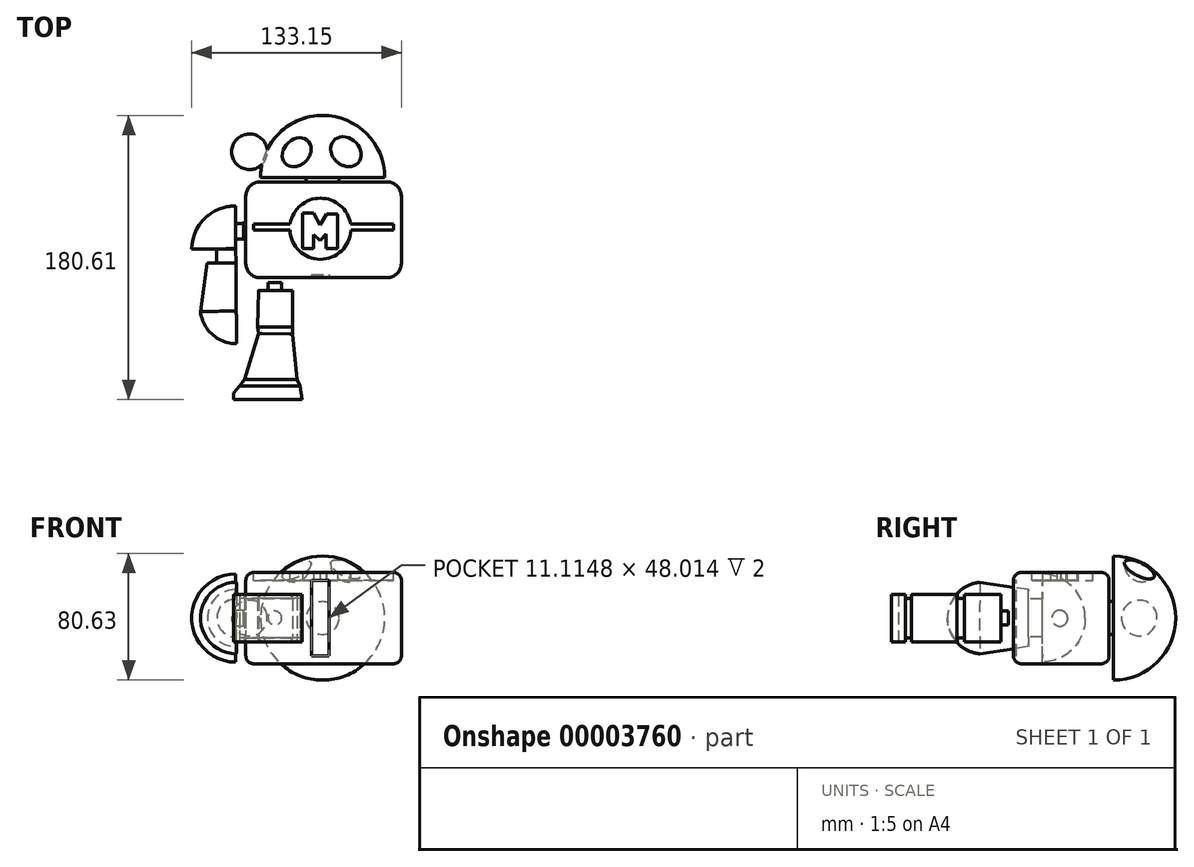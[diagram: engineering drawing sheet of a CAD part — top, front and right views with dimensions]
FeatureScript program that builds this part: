
annotation { "Feature Type Name" : "Feature", "Feature Type Description" : "" }
export const myFeature = defineFeature(function(context is Context, id is Id, definition is map)
    precondition{}
    {
        {
            var Q0;
            Q0=qCreatedBy(makeId("Top.planeOp"),FACE);
            var sketch = newSketch(context, id + "F0", { "sketchPlane" : qUnion([Q0])});
            skArc(sketch, "E0", {"start": v(39.44, 0) * mm, "mid": v(39.43, 0.3) * mm, "end": v(39.43, 0.59) * mm});
            skLineSegment(sketch, "E1", {"start": v(-39.44, 0) * mm, "end": v(0, 0) * mm});
            skLineSegment(sketch, "E2", {"start": v(0, 0) * mm, "end": v(0, 39.44) * mm});
            skArc(sketch, "E3", {"start": v(0, 39.44) * mm, "mid": v(-27.88, 27.88) * mm, "end": v(-39.44, 0) * mm});
            skSolve(sketch);
        }
        {
            var Q0;
            Q0=makeQuery(id+"F0.imprint","IMPRINT",FACE,{"disambiguationData":[TD([[makeQuery(id+"F0.imprint","IMPRINT",EDGE,{"derivedFrom":sQuery(id+"F0.wireOp",EDGE,"E1")}),1.0]])]});
            var Q1;
            Q1=sQuery(id+"F0.wireOp",EDGE,"E2");
            revolve(context, id + "F1", {"entities" : qUnion([Q0]), "axis" : qUnion([Q1]), "revolveType" : RevolveType.FULL});
        }
        {
            var Q0;
            Q0=qCreatedBy(makeId("Top.planeOp"),FACE);
            var sketch = newSketch(context, id + "F2", { "sketchPlane" : qUnion([Q0])});
            skCircle(sketch, "E4", {"center": v(-46.45, 16.3) * mm, "radius": 11.3 * mm});
            skLineSegment(sketch, "E5", {"start": v(-46.45, 27.6) * mm, "end": v(-46.45, 5) * mm});
            skSolve(sketch);
        }
        {
            var Q0;
            {var subQ0=sQuery(id+"F2.wireOp",EDGE,"E5");Q0=makeQuery(id+"F2.imprint","IMPRINT",FACE,{"disambiguationData":[TD([[makeQuery(id+"F2.imprint","IMPRINT",EDGE,{"derivedFrom":subQ0}),1.0]])]});}
            var Q1;
            Q1=sQuery(id+"F2.wireOp",EDGE,"E4");
            var Q2;
            Q2=sQuery(id+"F2.wireOp",EDGE,"E5");
            revolve(context, id + "F3", {"entities" : qUnion([Q0]), "surfaceEntities" : qUnion([Q1]), "axis" : qUnion([Q2]), "revolveType" : RevolveType.FULL});
        }
        {
            var Q0;
            Q0=makeQuery(id+"F1.opRevolve","SWEPT_BODY",BODY,{"disambiguationData":[OSD([sQuery(id+"F0.wireOp",EDGE,"E1"),sQuery(id+"F0.wireOp",EDGE,"E2"),sQuery(id+"F0.wireOp",EDGE,"E3")])]});
            transform(context, id + "F4", {"entities" : qUnion([Q0]), "transformType" : TransformType.COPY});
        }
        {
            var Q0;
            Q0=makeQuery(id+"F4.opPattern","COPY",BODY,{"derivedFrom":makeQuery(id+"F1.opRevolve","SWEPT_BODY",BODY,{"disambiguationData":[OSD([sQuery(id+"F0.wireOp",EDGE,"E1"),sQuery(id+"F0.wireOp",EDGE,"E2"),sQuery(id+"F0.wireOp",EDGE,"E3")])]}),"instanceName":"1"});
            var Q1;
            Q1=qCreatedBy(makeId("Origin.pointOp"),VERTEX);
            transform(context, id + "F5", {"entities" : qUnion([Q0]), "transformType" : TransformType.SCALE_UNIFORMLY, "scale" : 0.2, "makeCopy" : false, "scalePoint" : qUnion([Q1])});
        }
        {
            var Q0;
            Q0=makeQuery(id+"F3.opRevolve","SWEPT_BODY",BODY,{"disambiguationData":[OSD([sQuery(id+"F2.wireOp",EDGE,"E4"),sQuery(id+"F2.wireOp",EDGE,"E5")])]});
            transform(context, id + "F6", {"entities" : qUnion([Q0]), "transformType" : TransformType.TRANSLATION_3D, "dx" : 27.9 * mm, "dy" : 1.83 * mm, "dz" : 34.34 * mm, "makeCopy" : true});
        }
        {
            var Q0;
            Q0=makeQuery(id+"F6.opPattern","COPY",BODY,{"derivedFrom":makeQuery(id+"F3.opRevolve","SWEPT_BODY",BODY,{"disambiguationData":[OSD([sQuery(id+"F2.wireOp",EDGE,"E4"),sQuery(id+"F2.wireOp",EDGE,"E5")])]}),"instanceName":"1"});
            transform(context, id + "F7", {"entities" : qUnion([Q0]), "transformType" : TransformType.TRANSLATION_3D, "dx" : 35 * mm, "dy" : 0 * mm, "dz" : 0 * mm, "makeCopy" : true});
        }
        {
            var Q0;
            Q0=makeQuery(id+"F6.opPattern","COPY",BODY,{"derivedFrom":makeQuery(id+"F3.opRevolve","SWEPT_BODY",BODY,{"disambiguationData":[OSD([sQuery(id+"F2.wireOp",EDGE,"E4"),sQuery(id+"F2.wireOp",EDGE,"E5")])]}),"instanceName":"1"});
            var Q1;
            Q1=makeQuery(id+"F7.opPattern","COPY",BODY,{"derivedFrom":makeQuery(id+"F6.opPattern","COPY",BODY,{"derivedFrom":makeQuery(id+"F3.opRevolve","SWEPT_BODY",BODY,{"disambiguationData":[OSD([sQuery(id+"F2.wireOp",EDGE,"E4"),sQuery(id+"F2.wireOp",EDGE,"E5")])]}),"instanceName":"1"}),"instanceName":"1"});
            var Q2;
            Q2=makeQuery(id+"F1.opRevolve","SWEPT_BODY",BODY,{"disambiguationData":[OSD([sQuery(id+"F0.wireOp",EDGE,"E1"),sQuery(id+"F0.wireOp",EDGE,"E2"),sQuery(id+"F0.wireOp",EDGE,"E3")])]});
            booleanBodies(context, id + "F8", {"operationType" : BooleanOperationType.SUBTRACTION, "tools" : qUnion([Q0, Q1]), "targets" : qUnion([Q2])});
        }
        {
            var Q0;
            Q0=qCreatedBy(makeId("Top.planeOp"),FACE);
            var sketch = newSketch(context, id + "F9", { "sketchPlane" : qUnion([Q0])});
            skLineSegment(sketch, "E6.bottom", {"start": v(-39.75, -2.85) * mm, "end": v(41.03, -2.85) * mm});
            skLineSegment(sketch, "E6.top", {"start": v(-39.75, -63.63) * mm, "end": v(41.03, -63.63) * mm});
            skLineSegment(sketch, "E6.left", {"start": v(-48.75, -11.85) * mm, "end": v(-48.75, -54.63) * mm});
            skLineSegment(sketch, "E6.right", {"start": v(50.03, -11.85) * mm, "end": v(50.03, -54.63) * mm});
            skPoint(sketch, "E7.visualSharp", {"position": v(-48.75, -2.85) * mm});
            skArc(sketch, "E7.filletArc", {"start": v(-39.75, -2.85) * mm, "mid": v(-46.12, -5.49) * mm, "end": v(-48.75, -11.85) * mm});
            skPoint(sketch, "E8.visualSharp", {"position": v(50.03, -2.85) * mm});
            skArc(sketch, "E8.filletArc", {"start": v(50.03, -11.85) * mm, "mid": v(47.4, -5.49) * mm, "end": v(41.03, -2.85) * mm});
            skPoint(sketch, "E9.visualSharp", {"position": v(50.03, -63.63) * mm});
            skArc(sketch, "E9.filletArc", {"start": v(41.03, -63.63) * mm, "mid": v(47.4, -61) * mm, "end": v(50.03, -54.63) * mm});
            skPoint(sketch, "E10.visualSharp", {"position": v(-48.75, -63.63) * mm});
            skArc(sketch, "E10.filletArc", {"start": v(-48.75, -54.63) * mm, "mid": v(-46.12, -61) * mm, "end": v(-39.75, -63.63) * mm});
            skSolve(sketch);
        }
        {
            var Q0;
            Q0=makeQuery(id+"F9.imprint","IMPRINT",FACE,{"disambiguationData":[TD([[makeQuery(id+"F9.imprint","IMPRINT",EDGE,{"derivedFrom":sQuery(id+"F9.wireOp",EDGE,"E6.bottom")}),-1.0]])]});
            extrude(context, id + "F10", {"entities" : qUnion([Q0]), "endBound" : BoundingType.SYMMETRIC, "depth" : 58 * mm});
        }
        {
            var Q0;
            Q0=qCreatedBy(makeId("Top.planeOp"),FACE);
            var sketch = newSketch(context, id + "F11", { "sketchPlane" : qUnion([Q0])});
            skArc(sketch, "E11", {"start": v(-55.4, -18.13) * mm, "mid": v(-74.92, -26.07) * mm, "end": v(-83.12, -45.48) * mm});
            skLineSegment(sketch, "E12", {"start": v(-83.12, -45.48) * mm, "end": v(-67.17, -45.48) * mm});
            skLineSegment(sketch, "E13", {"start": v(-67.17, -45.48) * mm, "end": v(-67.17, -54.36) * mm});
            skLineSegment(sketch, "E14", {"start": v(-67.17, -54.36) * mm, "end": v(-73.25, -54.36) * mm});
            skLineSegment(sketch, "E15", {"start": v(-73.25, -54.36) * mm, "end": v(-77.56, -85.1) * mm});
            skArc(sketch, "E16", {"start": v(-77.56, -85.1) * mm, "mid": v(-70.06, -99.74) * mm, "end": v(-54.64, -105.5) * mm});
            skLineSegment(sketch, "E17", {"start": v(-54.64, -105.5) * mm, "end": v(-55.4, -18.13) * mm});
            skSolve(sketch);
        }
        {
            var Q0;
            Q0=makeQuery(id+"F11.imprint","IMPRINT",FACE,{"disambiguationData":[TD([[makeQuery(id+"F11.imprint","IMPRINT",EDGE,{"derivedFrom":sQuery(id+"F11.wireOp",EDGE,"E11")}),1.0]])]});
            var Q1;
            Q1=sQuery(id+"F11.wireOp",EDGE,"E17");
            revolve(context, id + "F12", {"entities" : qUnion([Q0]), "axis" : qUnion([Q1]), "revolveType" : RevolveType.SYMMETRIC, "angle" : 180 * degree});
        }
        {
            var Q0;
            Q0=qCreatedBy(makeId("Top.planeOp"),FACE);
            var sketch = newSketch(context, id + "F13", { "sketchPlane" : qUnion([Q0])});
            skLineSegment(sketch, "E18", {"start": v(-40.54, -71.66) * mm, "end": v(-19.06, -71.66) * mm});
            skLineSegment(sketch, "E19", {"start": v(-19.06, -71.66) * mm, "end": v(-19.06, -94.9) * mm});
            skLineSegment(sketch, "E20", {"start": v(-19.06, -94.9) * mm, "end": v(-41.36, -94.9) * mm});
            skLineSegment(sketch, "E21", {"start": v(-41.36, -94.9) * mm, "end": v(-40.54, -71.66) * mm});
            skLineSegment(sketch, "E22", {"start": v(-40.54, -99.07) * mm, "end": v(-49.65, -128.28) * mm});
            skLineSegment(sketch, "E23", {"start": v(-49.65, -128.28) * mm, "end": v(-16.26, -128.28) * mm});
            skLineSegment(sketch, "E24", {"start": v(-16.26, -128.28) * mm, "end": v(-19.1, -99.53) * mm});
            skLineSegment(sketch, "E25", {"start": v(-19.1, -99.53) * mm, "end": v(-40.54, -99.07) * mm});
            skLineSegment(sketch, "E26", {"start": v(-14.37, -132.38) * mm, "end": v(-52.7, -132.38) * mm});
            skLineSegment(sketch, "E27", {"start": v(-52.7, -132.38) * mm, "end": v(-56.6, -136.81) * mm});
            skLineSegment(sketch, "E28", {"start": v(-56.6, -136.81) * mm, "end": v(-56.6, -141.17) * mm});
            skLineSegment(sketch, "E29", {"start": v(-56.6, -141.17) * mm, "end": v(-13.15, -141.17) * mm});
            skLineSegment(sketch, "E30", {"start": v(-13.15, -141.17) * mm, "end": v(-14.37, -132.38) * mm});
            skLineSegment(sketch, "E31", {"start": v(-41.36, -94.9) * mm, "end": v(-40.54, -99.07) * mm});
            skLineSegment(sketch, "E32", {"start": v(-49.65, -128.28) * mm, "end": v(-52.7, -132.38) * mm});
            skLineSegment(sketch, "E33", {"start": v(-14.37, -132.38) * mm, "end": v(-16.26, -128.28) * mm});
            skLineSegment(sketch, "E34", {"start": v(-19.1, -99.53) * mm, "end": v(-19.06, -94.9) * mm});
            skSolve(sketch);
        }
        {
            var Q0;
            Q0=makeQuery(id+"F13.imprint","IMPRINT",FACE,{"disambiguationData":[TD([[makeQuery(id+"F13.imprint","IMPRINT",EDGE,{"derivedFrom":sQuery(id+"F13.wireOp",EDGE,"E26")}),1.0]])]});
            var Q1;
            Q1=makeQuery(id+"F13.imprint","IMPRINT",FACE,{"disambiguationData":[TD([[makeQuery(id+"F13.imprint","IMPRINT",EDGE,{"derivedFrom":sQuery(id+"F13.wireOp",EDGE,"E22")}),1.0]])]});
            var Q2;
            Q2=makeQuery(id+"F13.imprint","IMPRINT",FACE,{"disambiguationData":[TD([[makeQuery(id+"F13.imprint","IMPRINT",EDGE,{"derivedFrom":sQuery(id+"F13.wireOp",EDGE,"E18")}),-1.0]])]});
            extrude(context, id + "F14", {"entities" : qUnion([Q0, Q1, Q2]), "endBound" : BoundingType.SYMMETRIC, "depth" : 30 * mm});
        }
        {
            var Q0;
            Q0=makeQuery(id+"F13.imprint","IMPRINT",FACE,{"disambiguationData":[TD([[makeQuery(id+"F13.imprint","IMPRINT",EDGE,{"derivedFrom":sQuery(id+"F13.wireOp",EDGE,"E20")}),1.0]])]});
            var Q1;
            Q1=makeQuery(id+"F13.imprint","IMPRINT",FACE,{"disambiguationData":[TD([[makeQuery(id+"F13.imprint","IMPRINT",EDGE,{"derivedFrom":sQuery(id+"F13.wireOp",EDGE,"E23")}),-1.0]])]});
            extrude(context, id + "F15", {"entities" : qUnion([Q0, Q1]), "endBound" : BoundingType.SYMMETRIC, "depth" : 25 * mm});
        }
        {
            var Q0;
            Q0=makeQuery(id+"F10.opExtrude","CAP_FACE",FACE,{"disambiguationData":[OSD([sQuery(id+"F9.wireOp",EDGE,"E6.bottom"),sQuery(id+"F9.wireOp",EDGE,"E6.top"),sQuery(id+"F9.wireOp",EDGE,"E6.left"),sQuery(id+"F9.wireOp",EDGE,"E6.right"),sQuery(id+"F9.wireOp",EDGE,"E7.filletArc"),sQuery(id+"F9.wireOp",EDGE,"E8.filletArc"),sQuery(id+"F9.wireOp",EDGE,"E9.filletArc"),sQuery(id+"F9.wireOp",EDGE,"E10.filletArc")])],"isStart":false});
            fillet(context, id + "F16", {"entities" : qUnion([Q0]), "radius" : 5 * mm, "tangentPropagation" : true, "allowEdgeOverflow" : false});
        }
        {
            var Q0;
            Q0=makeQuery(id+"F10.opExtrude","CAP_FACE",FACE,{"disambiguationData":[OSD([sQuery(id+"F9.wireOp",EDGE,"E6.bottom"),sQuery(id+"F9.wireOp",EDGE,"E6.top"),sQuery(id+"F9.wireOp",EDGE,"E6.left"),sQuery(id+"F9.wireOp",EDGE,"E6.right"),sQuery(id+"F9.wireOp",EDGE,"E7.filletArc"),sQuery(id+"F9.wireOp",EDGE,"E8.filletArc"),sQuery(id+"F9.wireOp",EDGE,"E9.filletArc"),sQuery(id+"F9.wireOp",EDGE,"E10.filletArc")])],"isStart":true});
            fillet(context, id + "F17", {"entities" : qUnion([Q0]), "radius" : 5 * mm, "tangentPropagation" : true, "allowEdgeOverflow" : false});
        }
        {
            var Q0;
            Q0=makeQuery(id+"F14.opExtrude","CAP_EDGE",EDGE,{"disambiguationData":[OSD([sQuery(id+"F13.wireOp",EDGE,"E21")])],"isStart":false});
            var Q1;
            Q1=makeQuery(id+"F14.opExtrude","CAP_EDGE",EDGE,{"disambiguationData":[OSD([sQuery(id+"F13.wireOp",EDGE,"E19")])],"isStart":false});
            var Q2;
            Q2=makeQuery(id+"F14.opExtrude","CAP_EDGE",EDGE,{"disambiguationData":[OSD([sQuery(id+"F13.wireOp",EDGE,"E19")])],"isStart":true});
            var Q3;
            Q3=makeQuery(id+"F14.opExtrude","CAP_EDGE",EDGE,{"disambiguationData":[OSD([sQuery(id+"F13.wireOp",EDGE,"E21")])],"isStart":true});
            fillet(context, id + "F18", {"entities" : qUnion([Q0, Q1, Q2, Q3]), "radius" : 3 * mm, "allowEdgeOverflow" : false});
        }
        {
            var Q0;
            Q0=makeQuery(id+"F14.opExtrude","CAP_EDGE",EDGE,{"disambiguationData":[OSD([sQuery(id+"F13.wireOp",EDGE,"E22")])],"isStart":false});
            var Q1;
            Q1=makeQuery(id+"F14.opExtrude","CAP_EDGE",EDGE,{"disambiguationData":[OSD([sQuery(id+"F13.wireOp",EDGE,"E24")])],"isStart":false});
            var Q2;
            Q2=makeQuery(id+"F14.opExtrude","CAP_EDGE",EDGE,{"disambiguationData":[OSD([sQuery(id+"F13.wireOp",EDGE,"E24")])],"isStart":true});
            var Q3;
            Q3=makeQuery(id+"F14.opExtrude","CAP_EDGE",EDGE,{"disambiguationData":[OSD([sQuery(id+"F13.wireOp",EDGE,"E22")])],"isStart":true});
            fillet(context, id + "F19", {"entities" : qUnion([Q0, Q1, Q2, Q3]), "radius" : 2 * mm, "allowEdgeOverflow" : false});
        }
        {
            var Q0;
            Q0=makeQuery(id+"F10.opExtrude","CAP_FACE",FACE,{"disambiguationData":[OSD([sQuery(id+"F9.wireOp",EDGE,"E6.bottom"),sQuery(id+"F9.wireOp",EDGE,"E6.top"),sQuery(id+"F9.wireOp",EDGE,"E6.left"),sQuery(id+"F9.wireOp",EDGE,"E6.right"),sQuery(id+"F9.wireOp",EDGE,"E7.filletArc"),sQuery(id+"F9.wireOp",EDGE,"E8.filletArc"),sQuery(id+"F9.wireOp",EDGE,"E9.filletArc"),sQuery(id+"F9.wireOp",EDGE,"E10.filletArc")])],"isStart":false});
            var sketch = newSketch(context, id + "F20", { "sketchPlane" : qUnion([Q0])});
            skCircle(sketch, "E35", {"center": v(-1.4, -32.58) * mm, "radius": 19.4 * mm});
            skLineSegment(sketch, "E36", {"start": v(-20.56, -29.48) * mm, "end": v(-43.75, -29.48) * mm});
            skLineSegment(sketch, "E37", {"start": v(-43.75, -29.48) * mm, "end": v(-43.75, -33.24) * mm});
            skLineSegment(sketch, "E38", {"start": v(-43.75, -33.24) * mm, "end": v(-20.8, -33.24) * mm});
            skLineSegment(sketch, "E39", {"start": v(17.98, -33.48) * mm, "end": v(45.03, -33.48) * mm});
            skLineSegment(sketch, "E40", {"start": v(45.03, -33.48) * mm, "end": v(45.03, -29.48) * mm});
            skLineSegment(sketch, "E41", {"start": v(45.03, -29.48) * mm, "end": v(17.76, -29.48) * mm});
            skSolve(sketch);
        }
        {
            var Q0;
            Q0 = qSketchRegion(id + "F20", true);
            extrude(context, id + "F21", {"entities" : qUnion([Q0]), "operationType" : NewBodyOperationType.REMOVE, "oppositeDirection" : true, "depth" : 5 * mm});
        }
        {
            var Q0;
            Q0=makeQuery(id+"F21.boolean.opBoolean","COPY",FACE,{"derivedFrom":makeQuery(id+"F21.opExtrude","CAP_FACE",FACE,{"disambiguationData":[OSD([sQuery(id+"F20.wireOp",EDGE,"E35")])],"isStart":false})});
            var sketch = newSketch(context, id + "F22", { "sketchPlane" : qUnion([Q0])});
            skLineSegment(sketch, "E42", {"start": v(-12.61, -45.17) * mm, "end": v(-12.61, -22.72) * mm});
            skLineSegment(sketch, "E43", {"start": v(-12.61, -22.72) * mm, "end": v(-5.87, -22.72) * mm});
            skLineSegment(sketch, "E44", {"start": v(-5.87, -22.72) * mm, "end": v(-1.58, -30.17) * mm});
            skLineSegment(sketch, "E45", {"start": v(-1.58, -30.17) * mm, "end": v(2.66, -23.15) * mm});
            skLineSegment(sketch, "E46", {"start": v(2.66, -23.15) * mm, "end": v(9.67, -23.15) * mm});
            skLineSegment(sketch, "E47", {"start": v(9.67, -23.15) * mm, "end": v(9.67, -45.14) * mm});
            skLineSegment(sketch, "E48", {"start": v(9.67, -45.14) * mm, "end": v(2.32, -45.14) * mm});
            skLineSegment(sketch, "E49", {"start": v(2.32, -45.14) * mm, "end": v(2.32, -36.03) * mm});
            skLineSegment(sketch, "E50", {"start": v(2.32, -36.03) * mm, "end": v(-1.64, -40.08) * mm});
            skLineSegment(sketch, "E51", {"start": v(-1.64, -40.08) * mm, "end": v(-5.7, -36.1) * mm});
            skLineSegment(sketch, "E52", {"start": v(-5.7, -36.1) * mm, "end": v(-5.7, -45.17) * mm});
            skLineSegment(sketch, "E53", {"start": v(-5.7, -45.17) * mm, "end": v(-12.61, -45.17) * mm});
            skSolve(sketch);
        }
        {
            var Q0;
            Q0=makeQuery(id+"F22.imprint","IMPRINT",FACE,{"disambiguationData":[TD([[makeQuery(id+"F22.imprint","IMPRINT",EDGE,{"derivedFrom":sQuery(id+"F22.wireOp",EDGE,"E42")}),-1.0]])]});
            extrude(context, id + "F23", {"entities" : qUnion([Q0]), "operationType" : NewBodyOperationType.ADD, "depth" : 5 * mm});
        }
        {
            var Q0;
            Q0=makeQuery(id+"F12.opRevolve","CAP_FACE",FACE,{"disambiguationData":[OSD([sQuery(id+"F11.wireOp",EDGE,"E11"),sQuery(id+"F11.wireOp",EDGE,"E12"),sQuery(id+"F11.wireOp",EDGE,"E13"),sQuery(id+"F11.wireOp",EDGE,"E14"),sQuery(id+"F11.wireOp",EDGE,"E15"),sQuery(id+"F11.wireOp",EDGE,"E16"),sQuery(id+"F11.wireOp",EDGE,"E17")])],"isStart":true});
            var sketch = newSketch(context, id + "F24", { "sketchPlane" : qUnion([Q0])});
            skCircle(sketch, "E54", {"center": v(-33.72, -0.16) * mm, "radius": 5.05 * mm});
            skSolve(sketch);
        }
        {
            var Q0;
            Q0=makeQuery(id+"F24.imprint","IMPRINT",FACE,{"disambiguationData":[TD([[makeQuery(id+"F24.imprint","IMPRINT",EDGE,{"derivedFrom":sQuery(id+"F24.wireOp",EDGE,"E54")}),1.0]])]});
            extrude(context, id + "F25", {"entities" : qUnion([Q0]), "operationType" : NewBodyOperationType.ADD, "depth" : 5 * mm});
        }
        {
            var Q0;
            Q0=makeQuery(id+"F14.opExtrude","SWEPT_FACE",FACE,{"disambiguationData":[OSD([sQuery(id+"F13.wireOp",EDGE,"E18")])]});
            var sketch = newSketch(context, id + "F26", { "sketchPlane" : qUnion([Q0])});
            skCircle(sketch, "E55", {"center": v(30.37, 0) * mm, "radius": 4.4 * mm});
            skSolve(sketch);
        }
        {
            var Q0;
            Q0=makeQuery(id+"F26.imprint","IMPRINT",FACE,{"disambiguationData":[TD([[makeQuery(id+"F26.imprint","IMPRINT",EDGE,{"derivedFrom":sQuery(id+"F26.wireOp",EDGE,"E55")}),1.0]])]});
            extrude(context, id + "F27", {"entities" : qUnion([Q0]), "operationType" : NewBodyOperationType.ADD, "depth" : 5 * mm});
        }
        {
            var Q0;
            Q0=makeQuery(id+"F1.opRevolve","SWEPT_FACE",FACE,{"disambiguationData":[OSD([sQuery(id+"F0.wireOp",EDGE,"E1")])]});
            var sketch = newSketch(context, id + "F28", { "sketchPlane" : qUnion([Q0])});
            skCircle(sketch, "E56", {"center": v(0, 0) * mm, "radius": 10.44 * mm});
            skSolve(sketch);
        }
        {
            var Q0;
            Q0 = qSketchRegion(id + "F28", true);
            extrude(context, id + "F29", {"entities" : qUnion([Q0]), "operationType" : NewBodyOperationType.ADD, "depth" : 5 * mm});
        }
        {
            var Q0;
            Q0=makeQuery(id+"F10.opExtrude","SWEPT_FACE",FACE,{"disambiguationData":[OSD([sQuery(id+"F9.wireOp",EDGE,"E6.top")])]});
            var sketch = newSketch(context, id + "F30", { "sketchPlane" : qUnion([Q0])});
            skLineSegment(sketch, "E57.bottom", {"start": v(-7.02, -24) * mm, "end": v(4.1, -24) * mm});
            skLineSegment(sketch, "E57.top", {"start": v(-7.02, 24) * mm, "end": v(4.1, 24) * mm});
            skLineSegment(sketch, "E57.left", {"start": v(-7.02, -24) * mm, "end": v(-7.02, 24) * mm});
            skLineSegment(sketch, "E57.right", {"start": v(4.1, -24) * mm, "end": v(4.1, 24) * mm});
            skSolve(sketch);
        }
        {
            var Q0;
            Q0=makeQuery(id+"F30.imprint","IMPRINT",FACE,{"disambiguationData":[TD([[makeQuery(id+"F30.imprint","IMPRINT",EDGE,{"derivedFrom":sQuery(id+"F30.wireOp",EDGE,"E57.bottom")}),1.0]])]});
            extrude(context, id + "F31", {"entities" : qUnion([Q0]), "operationType" : NewBodyOperationType.REMOVE, "oppositeDirection" : true, "depth" : 2 * mm});
        }
    });
